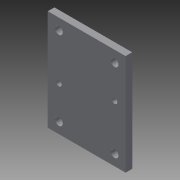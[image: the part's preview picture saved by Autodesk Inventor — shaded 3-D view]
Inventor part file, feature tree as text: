
AUTODESK INVENTOR PART (.ipt)
format: ipt  version: 2015 (Build 190159000, 159)  size: 104,448 bytes
history: native  units: mm
features: extrude x1, sketch x1
ambient origin geometry x8: Origin, YZ Plane, XZ Plane, XY Plane, X Axis, Y Axis, Z Axis, Center Point
bodies: Solid1 (feature_tree)
feature tree (2):
  extrude  "Extrusion1"  Depth=70.5mm
  sketch  "Sketch1"  dims[d6=5.0mm d9=70.5mm d41=70.5mm d42=91.5mm d43=10.0mm d44=10.0mm d45=7.0mm d46=10.0mm d47=10.0mm d48=90.0deg d50=7.0mm d51=10.0mm d52=10.0mm d53=7.0mm d54=10.0mm d55=10.0mm d56=7.0mm d60=30.0mm d61=30.0mm d62=5.0mm d63=5.0mm d65=6.0mm d66=0.0mm]
